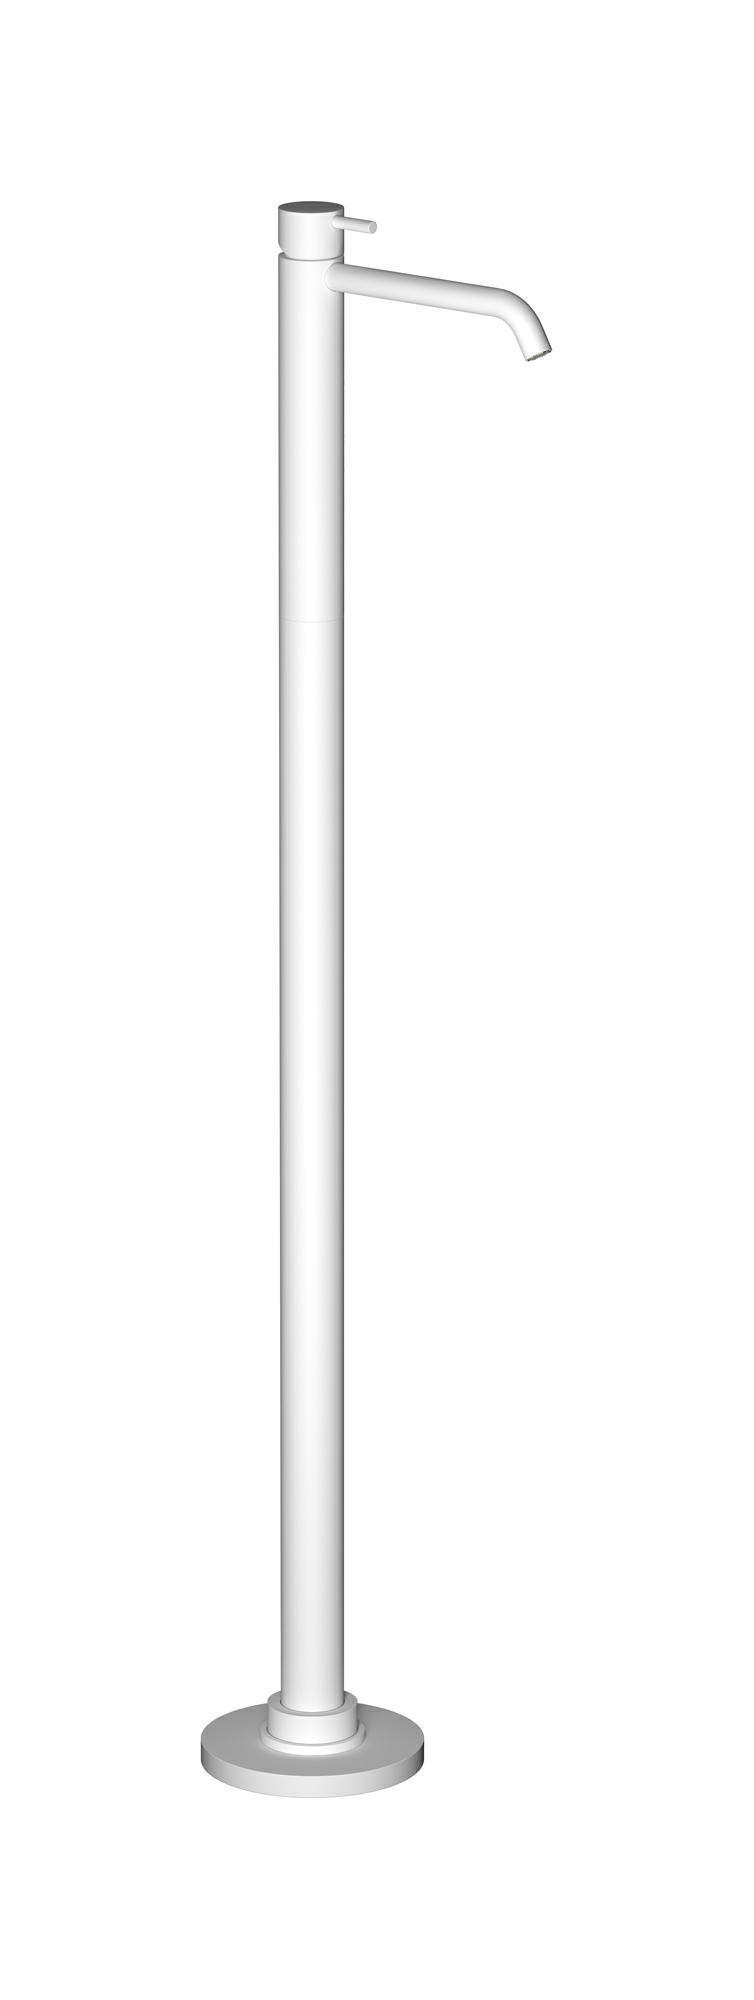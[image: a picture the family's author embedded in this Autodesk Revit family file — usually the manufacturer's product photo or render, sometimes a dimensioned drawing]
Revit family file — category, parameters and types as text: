
# Revit family: MT299
name_source: partatom
category: Apparecchi idraulici
units: mm (PartAtom-declared; Revit-internal decimal feet)

## family parameters
Basato su piano di lavoro = No
Condiviso = No
Mantieni orientamento annotazione = No
Numero OmniClass = 23.45.55.17
Punto di calcolo locali = No
Quota connettore circolare = Usa diametro
Sempre verticale = Sì
Taglio con vuoti quando caricato = No
Tipo di parte = Normale
Titolo OmniClass = Mixing Faucets

## types (13) — shared parameters
Cold water inlet = 10 mm  [stored 0.0328084 ft]
Commenti sul tipo = Washbasin mixer
Connessione CW = No
Connessione HW = No
Connessione di scarico = No
Connessione di ventilazione = No
Descrizione = Monohole freestanding washbasin mixer complete with drain
Hot water inlet = 10 mm  [stored 0.0328084 ft]
Produttore = IB Rubinetterie S.p.A.
URL = https://www.weareib.it
zero-valued in all types: Prospetto di default

## per-type parameters (varying)
| type | Finishes surface | Immagine tipo | Modello |
| Chrome | IB_Chrome | MT299CC.jpg | MT299CC |
| Brushed nickel | IB_Brushed nickel | MT299SS.jpg | MT299SS |
| Matt black | IB_matt black | MT299NP.jpg | MT299NP |
| Matt white | IB_matt white | MT299BO.jpg | MT299BO |
| Natural brass | IB_Brass | MT299ON.jpg | MT299ON |
| Black chrome | IB_Black chrome | MT299CF.jpg | MT299CF |
| Brushed black chrome | IB_Brushed black chrome | MT299CS.jpg | MT299CS |
| Pale gold | IB_Pale gold | MT299II.jpg | MT299II |
| Brushed pale gold | IB_brushed pale gold | MT299IS.jpg | MT299IS |
| Rose gold | IB_Rose gold | MT299RS.jpg | MT299RS |
| Brushed rose gold | IB_Brushed rose gold | MT299SR.jpg | MT299SR |
| Gold | IB_gold | MT299OO.jpg | MT299OO |
| Brushed gold | IB_brushed gold | MT299OS.jpg | MT299OS |

note: [stored X ft] marks values corroborated as IEEE doubles in the binary element streams (Revit-internal decimal feet)
